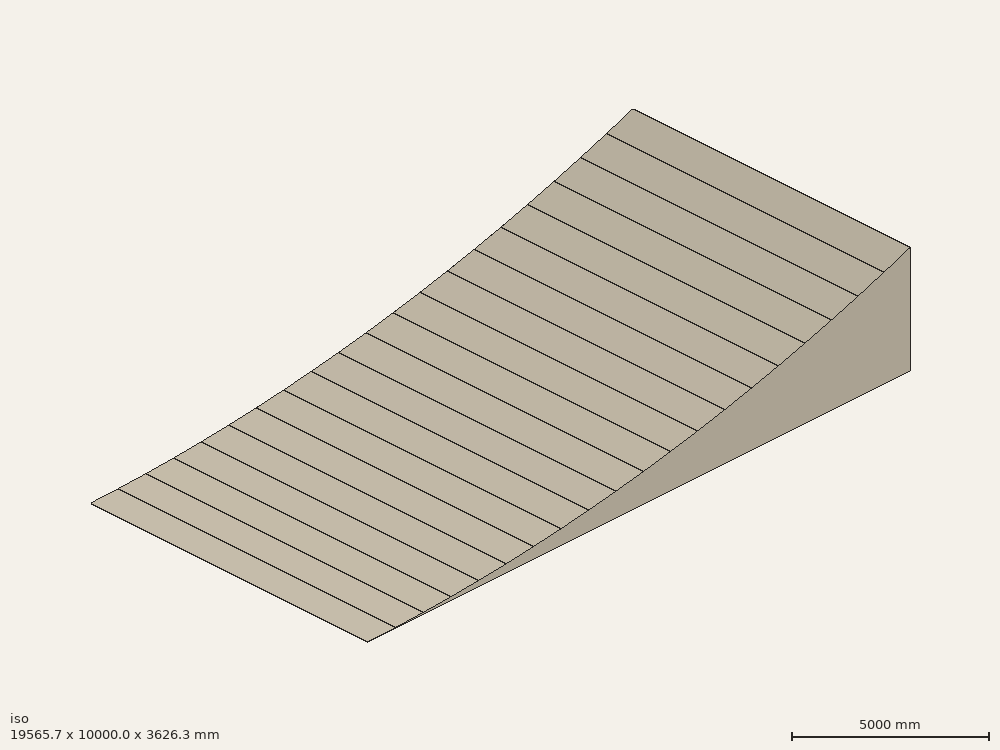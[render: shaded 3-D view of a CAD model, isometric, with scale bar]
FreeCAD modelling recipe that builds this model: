
FCSTD DOCUMENT  (FreeCAD 0.19R24291 (Git))
Label: VariablePlane01
License: All rights reserved
LicenseURL: http://en.wikipedia.org/wiki/All_rights_reserved
objects: Sketcher::SketchObject×1, Part::Extrusion×1
note: 2 computed .brp shape members not serialized (recipe doc carries the construction recipe); baked Part::Feature solids carry a one-line shape summary decoded from their .brp

FEATURE [Sketcher::SketchObject] Sketch
  FullyConstrained = true
  Placement = pos=(0,0,0) rot=(-1,0,0;4.71239rad)
  sketch-geometry (22):
    g0: LineSegment StartX=0 StartY=0 StartZ=0 EndX=999.848 EndY=17.4524 EndZ=0
    g1: LineSegment StartX=999.848 StartY=17.4524 StartZ=0 EndX=1999.24 EndY=52.3519 EndZ=0
    g2: LineSegment StartX=1999.24 StartY=52.3519 StartZ=0 EndX=2997.87 EndY=104.688 EndZ=0
    g3: LineSegment StartX=2997.87 StartY=104.688 StartZ=0 EndX=3995.43 EndY=174.444 EndZ=0
    g4: LineSegment StartX=3995.43 StartY=174.444 StartZ=0 EndX=4991.63 EndY=261.6 EndZ=0
    g5: LineSegment StartX=4991.63 StartY=261.6 StartZ=0 EndX=5986.15 EndY=366.129 EndZ=0
    g6: LineSegment StartX=5986.15 StartY=366.129 StartZ=0 EndX=6978.69 EndY=487.998 EndZ=0
    g7: LineSegment StartX=6978.69 StartY=487.998 StartZ=0 EndX=7968.96 EndY=627.171 EndZ=0
    g8: LineSegment StartX=7968.96 StartY=627.171 StartZ=0 EndX=8956.65 EndY=783.605 EndZ=0
    g9: LineSegment StartX=8956.65 StartY=783.605 StartZ=0 EndX=9941.46 EndY=957.254 EndZ=0
    g10: LineSegment StartX=9941.46 StartY=957.254 StartZ=0 EndX=10923.1 EndY=1148.06 EndZ=0
    g11: LineSegment StartX=10923.1 StartY=1148.06 StartZ=0 EndX=11901.2 EndY=1355.97 EndZ=0
    g12: LineSegment StartX=11901.2 StartY=1355.97 StartZ=0 EndX=12875.6 EndY=1580.93 EndZ=0
    g13: LineSegment StartX=12875.6 StartY=1580.93 StartZ=0 EndX=13845.9 EndY=1822.85 EndZ=0
    g14: LineSegment StartX=13845.9 StartY=1822.85 StartZ=0 EndX=14811.8 EndY=2081.67 EndZ=0
    g15: LineSegment StartX=14811.8 StartY=2081.67 StartZ=0 EndX=15773.1 EndY=2357.3 EndZ=0
    g16: LineSegment StartX=15773.1 StartY=2357.3 StartZ=0 EndX=16729.4 EndY=2649.68 EndZ=0
    g17: LineSegment StartX=16729.4 StartY=2649.68 StartZ=0 EndX=17680.4 EndY=2958.69 EndZ=0
    g18: LineSegment StartX=17680.4 StartY=2958.69 StartZ=0 EndX=18626 EndY=3284.26 EndZ=0
    g19: LineSegment StartX=18626 StartY=3284.26 StartZ=0 EndX=19565.7 EndY=3626.28 EndZ=0
    g20: LineSegment StartX=19565.7 StartY=3626.28 StartZ=0 EndX=19565.7 EndY=0 EndZ=0
    g21: LineSegment StartX=19565.7 StartY=0 StartZ=0 EndX=0 EndY=0 EndZ=0
  constraints (65):
    c: Coincident(g0,g-1)
    c: Distance(g0) = 1000
    c: Angle(g0) = 0.0174533
    c: Coincident(g1,g0)
    c: Distance(g1) = 1000
    c: Angle(g1) = 0.0349066
    c: Coincident(g2,g1)
    c: Distance(g2) = 1000
    c: Angle(g2) = 0.0523599
    c: Coincident(g3,g2)
    c: Distance(g3) = 1000
    c: Angle(g3) = 0.0698132
    c: Coincident(g4,g3)
    c: Distance(g4) = 1000
    c: Angle(g4) = 0.0872665
    c: Coincident(g5,g4)
    c: Distance(g5) = 1000
    c: Angle(g5) = 0.10472
    c: Coincident(g6,g5)
    c: Distance(g6) = 1000
    c: Angle(g6) = 0.122173
    c: Coincident(g7,g6)
    c: Distance(g7) = 1000
    c: Angle(g7) = 0.139626
    c: Coincident(g8,g7)
    c: Distance(g8) = 1000
    c: Angle(g8) = 0.15708
    c: Coincident(g9,g8)
    c: Distance(g9) = 1000
    c: Angle(g9) = 0.174533
    c: Coincident(g10,g9)
    c: Distance(g10) = 1000
    c: Angle(g10) = 0.191986
    c: Coincident(g11,g10)
    c: Distance(g11) = 1000
    c: Angle(g11) = 0.20944
    c: Coincident(g12,g11)
    c: Distance(g12) = 1000
    c: Angle(g12) = 0.226893
    c: Coincident(g13,g12)
    c: Distance(g13) = 1000
    c: Angle(g13) = 0.244346
    c: Coincident(g14,g13)
    c: Distance(g14) = 1000
    c: Angle(g14) = 0.261799
    c: Coincident(g15,g14)
    c: Distance(g15) = 1000
    c: Angle(g15) = 0.279253
    c: Coincident(g16,g15)
    c: Distance(g16) = 1000
    c: Angle(g16) = 0.296706
    c: Coincident(g17,g16)
    c: Distance(g17) = 1000
    c: Angle(g17) = 0.314159
    c: Coincident(g18,g17)
    c: Distance(g18) = 1000
    c: Angle(g18) = 0.331613
    c: Coincident(g19,g18)
    c: Distance(g19) = 1000
    c: Angle(g19) = 0.349066
    c: Coincident(g20,g19)
    c: PointOnObject(g20,g-1)
    c: Angle(g20) = -1.5708
    c: Coincident(g21,g20)
    c: Coincident(g21,g0)
FEATURE [Part::Extrusion] Extrude
  Base = -> Sketch
  Dir = (0,-1,3e-16)
  DirMode = 2
  FaceMakerClass = Part::FaceMakerBullseye
  LengthFwd = 10000
  LengthRev = 0
  Solid = true
  Symmetric = true
